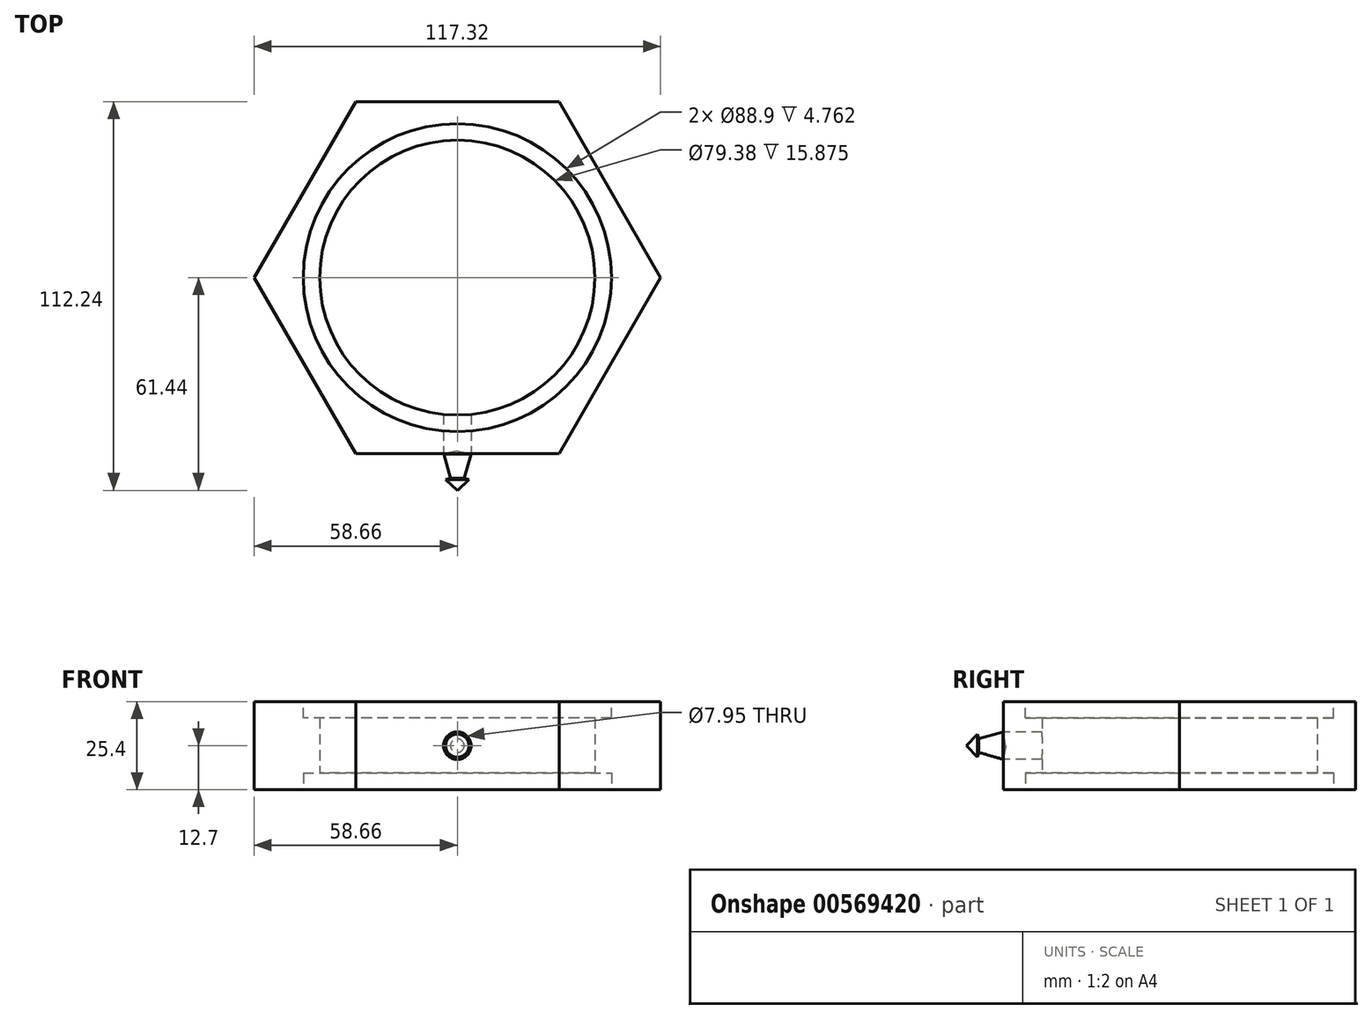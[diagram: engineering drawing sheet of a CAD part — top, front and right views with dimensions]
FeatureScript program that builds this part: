
annotation { "Feature Type Name" : "Feature", "Feature Type Description" : "" }
export const myFeature = defineFeature(function(context is Context, id is Id, definition is map)
    precondition{}
    {
        {
            var Q0;
            Q0=qCreatedBy(makeId("Top.planeOp"),FACE);
            var sketch = newSketch(context, id + "F0", { "sketchPlane" : qUnion([Q0])});
            skCircle(sketch, "E0.cCircle", {"center": v(0, 0) * mm, "radius": 50.8 * mm, "construction": true});
            skLineSegment(sketch, "E0.0", {"start": v(-29.33, 50.8) * mm, "end": v(29.33, 50.8) * mm});
            skLineSegment(sketch, "E0.1", {"start": v(29.33, 50.8) * mm, "end": v(58.66, 0) * mm});
            skLineSegment(sketch, "E0.2", {"start": v(58.66, 0) * mm, "end": v(29.33, -50.8) * mm});
            skLineSegment(sketch, "E0.3", {"start": v(29.33, -50.8) * mm, "end": v(-29.33, -50.8) * mm});
            skLineSegment(sketch, "E0.4", {"start": v(-29.33, -50.8) * mm, "end": v(-58.66, 0) * mm});
            skLineSegment(sketch, "E0.5", {"start": v(-58.66, 0) * mm, "end": v(-29.33, 50.8) * mm});
            skPoint(sketch, "E0.0.midPoint", {"position": v(0, 50.8) * mm});
            skCircle(sketch, "E1", {"center": v(0, 0) * mm, "radius": 39.69 * mm});
            skSolve(sketch);
        }
        {
            var Q0;
            Q0=makeQuery(id+"F0.imprint","IMPRINT",FACE,{"disambiguationData":[TD([[makeQuery(id+"F0.imprint","IMPRINT",EDGE,{"derivedFrom":sQuery(id+"F0.wireOp",EDGE,"E0.0")}),-1.0]])]});
            extrude(context, id + "F1", {"entities" : qUnion([Q0]), "endBound" : BoundingType.SYMMETRIC, "depth" : 25.4 * mm, "offsetDistance" : 25.4 * mm});
        }
        {
            var Q0;
            Q0=makeQuery(id+"F1.opExtrude","CAP_FACE",FACE,{"disambiguationData":[OSD([sQuery(id+"F0.wireOp",EDGE,"E0.0"),sQuery(id+"F0.wireOp",EDGE,"E0.1"),sQuery(id+"F0.wireOp",EDGE,"E0.2"),sQuery(id+"F0.wireOp",EDGE,"E0.3"),sQuery(id+"F0.wireOp",EDGE,"E0.4"),sQuery(id+"F0.wireOp",EDGE,"E0.5"),sQuery(id+"F0.wireOp",EDGE,"E1")])],"isStart":false});
            var sketch = newSketch(context, id + "F2", { "sketchPlane" : qUnion([Q0])});
            skCircle(sketch, "E2", {"center": v(0, 0) * mm, "radius": 44.45 * mm});
            skSolve(sketch);
        }
        {
            var Q0;
            Q0=makeQuery(id+"F2.imprint","IMPRINT",FACE,{"disambiguationData":[TD([[makeQuery(id+"F2.imprint","IMPRINT",EDGE,{"derivedFrom":sQuery(id+"F2.wireOp",EDGE,"E2")}),1.0]])]});
            extrude(context, id + "F3", {"entities" : qUnion([Q0]), "operationType" : NewBodyOperationType.REMOVE, "oppositeDirection" : true, "depth" : 4.76 * mm, "offsetDistance" : 25.4 * mm});
        }
        {
            var Q0;
            Q0=makeQuery(id+"F1.opExtrude","CAP_FACE",FACE,{"disambiguationData":[OSD([sQuery(id+"F0.wireOp",EDGE,"E0.0"),sQuery(id+"F0.wireOp",EDGE,"E0.1"),sQuery(id+"F0.wireOp",EDGE,"E0.2"),sQuery(id+"F0.wireOp",EDGE,"E0.3"),sQuery(id+"F0.wireOp",EDGE,"E0.4"),sQuery(id+"F0.wireOp",EDGE,"E0.5"),sQuery(id+"F0.wireOp",EDGE,"E1")])],"isStart":true});
            var sketch = newSketch(context, id + "F4", { "sketchPlane" : qUnion([Q0])});
            skCircle(sketch, "E3", {"center": v(0, 0) * mm, "radius": 44.45 * mm});
            skSolve(sketch);
        }
        {
            var Q0;
            Q0=makeQuery(id+"F4.imprint","IMPRINT",FACE,{"disambiguationData":[TD([[makeQuery(id+"F4.imprint","IMPRINT",EDGE,{"derivedFrom":sQuery(id+"F4.wireOp",EDGE,"E3")}),1.0]])]});
            extrude(context, id + "F5", {"entities" : qUnion([Q0]), "operationType" : NewBodyOperationType.REMOVE, "oppositeDirection" : true, "depth" : 4.76 * mm, "offsetDistance" : 25.4 * mm});
        }
        {
            var Q0;
            Q0=makeQuery(id+"F1.opExtrude","SWEPT_FACE",FACE,{"disambiguationData":[OSD([sQuery(id+"F0.wireOp",EDGE,"E0.3")])]});
            var sketch = newSketch(context, id + "F6", { "sketchPlane" : qUnion([Q0])});
            skCircle(sketch, "E4", {"center": v(0, 0) * mm, "radius": 3.98 * mm});
            skSolve(sketch);
        }
        {
            var Q0;
            Q0 = qSketchRegion(id + "F6", true);
            extrude(context, id + "F7", {"entities" : qUnion([Q0]), "operationType" : NewBodyOperationType.REMOVE, "endBound" : BoundingType.UP_TO_NEXT, "oppositeDirection" : true, "depth" : 25.4 * mm, "offsetDistance" : 25.4 * mm});
        }
        {
            var Q0;
            Q0=qCreatedBy(makeId("Top.planeOp"),FACE);
            var sketch = newSketch(context, id + "F8", { "sketchPlane" : qUnion([Q0])});
            skLineSegment(sketch, "E5", {"start": v(-3.94, -50.9) * mm, "end": v(-1.97, -57.9) * mm});
            skLineSegment(sketch, "E6", {"start": v(-1.97, -57.9) * mm, "end": v(-3.35, -58.29) * mm});
            skLineSegment(sketch, "E7", {"start": v(-3.35, -58.29) * mm, "end": v(0, -61.44) * mm});
            skLineSegment(sketch, "E8", {"start": v(0, -61.44) * mm, "end": v(0, -50.11) * mm});
            skLineSegment(sketch, "E9", {"start": v(0, -50.11) * mm, "end": v(-3.94, -50.9) * mm});
            skSolve(sketch);
        }
        {
            var Q0;
            Q0=makeQuery(id+"F8.imprint","IMPRINT",FACE,{"disambiguationData":[TD([[makeQuery(id+"F8.imprint","IMPRINT",EDGE,{"derivedFrom":sQuery(id+"F8.wireOp",EDGE,"E5")}),1.0]])]});
            var Q1;
            Q1=sQuery(id+"F8.wireOp",EDGE,"E8");
            revolve(context, id + "F9", {"entities" : qUnion([Q0]), "axis" : qUnion([Q1]), "revolveType" : RevolveType.FULL});
        }
    });
